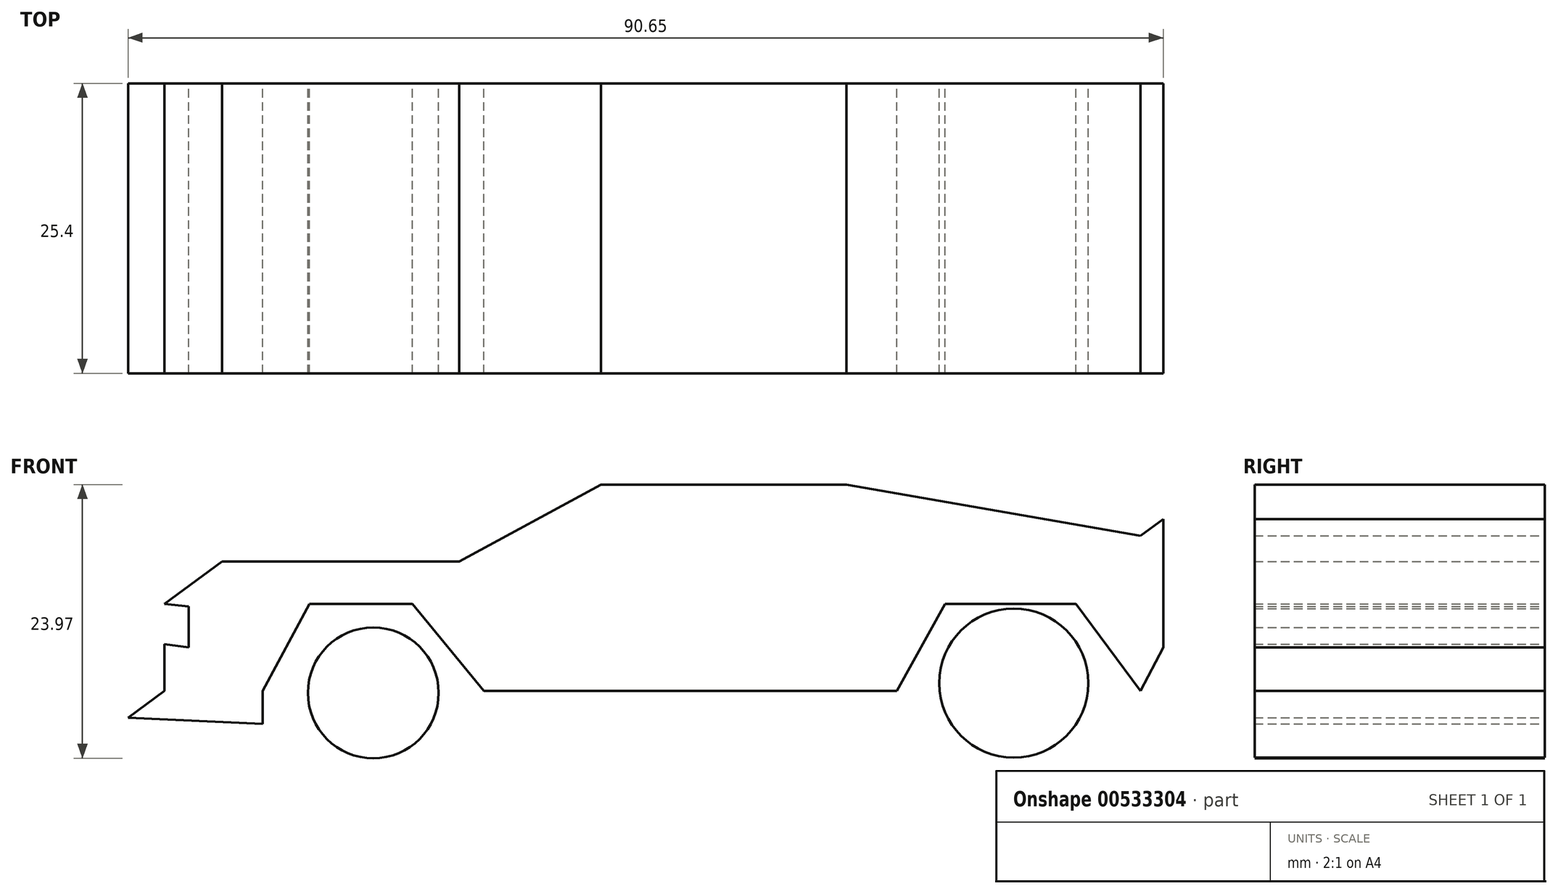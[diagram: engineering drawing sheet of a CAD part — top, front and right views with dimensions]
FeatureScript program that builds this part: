
annotation { "Feature Type Name" : "Feature", "Feature Type Description" : "" }
export const myFeature = defineFeature(function(context is Context, id is Id, definition is map)
    precondition{}
    {
        {
            var Q0;
            Q0=qCreatedBy(makeId("Front.planeOp"),FACE);
            var sketch = newSketch(context, id + "F0", { "sketchPlane" : qUnion([Q0])});
            skCircle(sketch, "E0", {"center": v(-38.6, 5.83) * mm, "radius": 5.71 * mm});
            skCircle(sketch, "E1", {"center": v(18.7, 5.83) * mm, "radius": 5.86 * mm});
            skLineSegment(sketch, "E2", {"start": v(-42.82, 13.47) * mm, "end": v(-33.77, 13.47) * mm});
            skLineSegment(sketch, "E3", {"start": v(-33.77, 13.47) * mm, "end": v(-27.54, 5.83) * mm});
            skLineSegment(sketch, "E4", {"start": v(-27.54, 5.83) * mm, "end": v(8.64, 5.83) * mm});
            skLineSegment(sketch, "E5", {"start": v(8.64, 5.83) * mm, "end": v(12.87, 13.47) * mm});
            skLineSegment(sketch, "E6", {"start": v(12.87, 13.47) * mm, "end": v(24.32, 13.47) * mm});
            skLineSegment(sketch, "E7", {"start": v(24.32, 13.47) * mm, "end": v(29.95, 5.83) * mm});
            skLineSegment(sketch, "E8", {"start": v(29.95, 5.83) * mm, "end": v(31.96, 9.65) * mm});
            skPoint(sketch, "E8.endSnap0", {"position": v(27.14, 9.65) * mm});
            skLineSegment(sketch, "E9", {"start": v(31.96, 9.65) * mm, "end": v(31.96, 13.47) * mm});
            skLineSegment(sketch, "E10", {"start": v(31.96, 13.47) * mm, "end": v(31.96, 20.9) * mm});
            skLineSegment(sketch, "E11", {"start": v(31.96, 20.9) * mm, "end": v(29.95, 19.43) * mm});
            skLineSegment(sketch, "E12", {"start": v(29.95, 19.43) * mm, "end": v(4.22, 23.92) * mm});
            skLineSegment(sketch, "E13", {"start": v(4.22, 23.92) * mm, "end": v(-17.29, 23.92) * mm});
            skLineSegment(sketch, "E14", {"start": v(-17.29, 23.92) * mm, "end": v(-29.68, 17.18) * mm});
            skLineSegment(sketch, "E15", {"start": v(-29.68, 17.18) * mm, "end": v(-50.46, 17.18) * mm});
            skLineSegment(sketch, "E16", {"start": v(-50.46, 17.18) * mm, "end": v(-55.5, 13.47) * mm});
            skLineSegment(sketch, "E17", {"start": v(-55.5, 13.47) * mm, "end": v(-53.39, 13.23) * mm});
            skLineSegment(sketch, "E18", {"start": v(-53.39, 13.23) * mm, "end": v(-53.39, 9.65) * mm});
            skLineSegment(sketch, "E19", {"start": v(-53.39, 9.65) * mm, "end": v(-55.5, 9.93) * mm});
            skLineSegment(sketch, "E20", {"start": v(-55.5, 9.93) * mm, "end": v(-55.5, 5.83) * mm});
            skLineSegment(sketch, "E21", {"start": v(-55.5, 5.83) * mm, "end": v(-58.7, 3.48) * mm});
            skLineSegment(sketch, "E22", {"start": v(-58.7, 3.48) * mm, "end": v(-46.9, 2.94) * mm});
            skLineSegment(sketch, "E23", {"start": v(-46.9, 2.94) * mm, "end": v(-46.9, 5.83) * mm});
            skLineSegment(sketch, "E24", {"start": v(-46.9, 5.83) * mm, "end": v(-42.82, 13.47) * mm});
            skSolve(sketch);
        }
        {
            var Q0;
            Q0=makeQuery(id+"F0.imprint","IMPRINT",FACE,{"disambiguationData":[TD([[makeQuery(id+"F0.imprint","IMPRINT",EDGE,{"derivedFrom":sQuery(id+"F0.wireOp",EDGE,"E2")}),1.0]])]});
            extrude(context, id + "F1", {"entities" : qUnion([Q0]), "depth" : 25.4 * mm, "offsetDistance" : 25.4 * mm});
        }
        {
            var Q0;
            Q0=qCreatedBy(makeId("Front.planeOp"),FACE);
            var sketch = newSketch(context, id + "F2", { "sketchPlane" : qUnion([Q0])});
            skCircle(sketch, "E25", {"center": v(-37.22, 5.67) * mm, "radius": 5.73 * mm});
            skCircle(sketch, "E26", {"center": v(17.92, 5.92) * mm, "radius": 6.86 * mm});
            skSolve(sketch);
        }
        {
            var Q0;
            Q0=makeQuery(id+"F2.imprint","IMPRINT",FACE,{"disambiguationData":[TD([[makeQuery(id+"F2.imprint","IMPRINT",EDGE,{"derivedFrom":sQuery(id+"F2.wireOp",EDGE,"E25")}),1.0]])]});
            extrude(context, id + "F3", {"entities" : qUnion([Q0]), "depth" : 25.4 * mm, "offsetDistance" : 25.4 * mm});
        }
        {
            var Q0;
            Q0=qCreatedBy(makeId("Front.planeOp"),FACE);
            var sketch = newSketch(context, id + "F4", { "sketchPlane" : qUnion([Q0])});
            skCircle(sketch, "E27", {"center": v(18.87, 6.53) * mm, "radius": 6.53 * mm});
            skSolve(sketch);
        }
        {
            var Q0;
            Q0=makeQuery(id+"F4.imprint","IMPRINT",FACE,{"disambiguationData":[TD([[makeQuery(id+"F4.imprint","IMPRINT",EDGE,{"derivedFrom":sQuery(id+"F4.wireOp",EDGE,"E27")}),1.0]])]});
            extrude(context, id + "F5", {"entities" : qUnion([Q0]), "depth" : 25.4 * mm, "offsetDistance" : 25.4 * mm});
        }
    });
